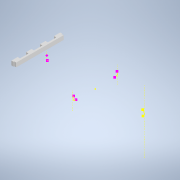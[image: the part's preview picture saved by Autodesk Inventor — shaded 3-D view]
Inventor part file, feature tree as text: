
AUTODESK INVENTOR PART (.ipt)
format: ipt  version: 2020 (Build 240168000, 168)  size: 294,400 bytes
history: native  units: mm
features: other x3, sketch x3, extrude x1, projected_geometry x1
ambient origin geometry x8: Origin, YZ Plane, XZ Plane, XY Plane, X Axis, Y Axis, Z Axis, Center Point
bodies: Solid1 (feature_tree)
feature tree (8):
  other  "Part9 scaled.ipt"
  extrude  "Extrusion1"  Depth=6.25mm TaperAngle=0.0deg
  other  "Solid1::Part9 scaled.ipt"
  other  "TaggingFeature1"
  sketch  "Sketch22"
  sketch  "Sketch23"
  sketch  "Sketch3"  dims[d0=10.0mm d1=6.25mm d2=0.0mm]
  projected_geometry  "Projected Loop1"
